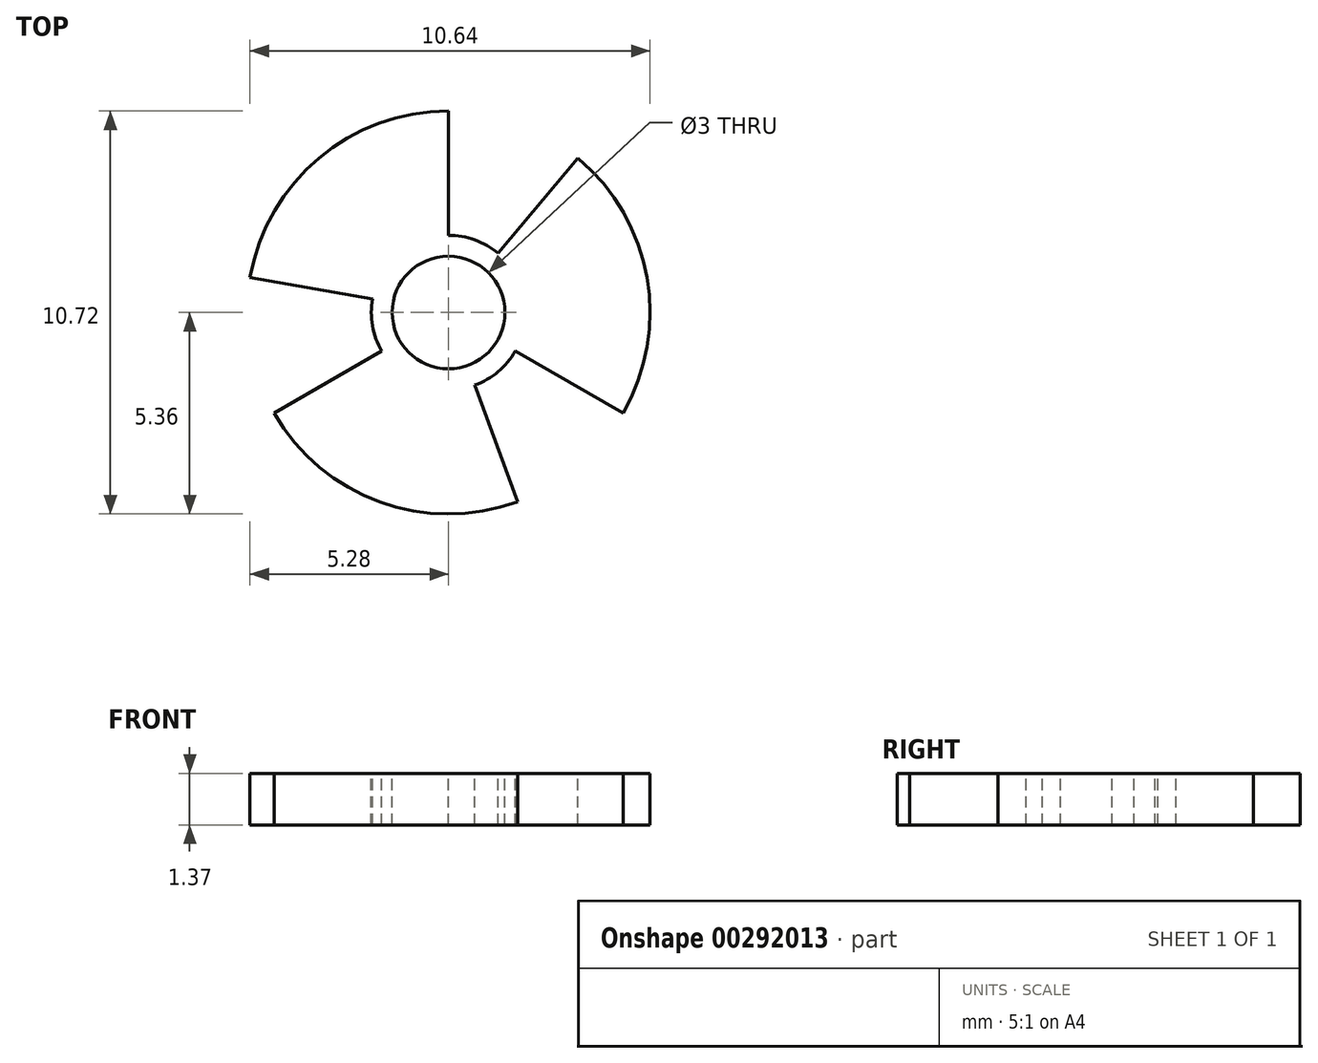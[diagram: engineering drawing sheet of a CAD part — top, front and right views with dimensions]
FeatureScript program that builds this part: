
annotation { "Feature Type Name" : "Feature", "Feature Type Description" : "" }
export const myFeature = defineFeature(function(context is Context, id is Id, definition is map)
    precondition{}
    {
        {
            var Q0;
            Q0=qCreatedBy(makeId("Top.planeOp"),FACE);
            var sketch = newSketch(context, id + "F0", { "sketchPlane" : qUnion([Q0])});
            skCircle(sketch, "E0", {"center": v(-28.46, 15.68) * mm, "radius": 28.38 * mm});
            skSolve(sketch);
        }
        {
            var Q0;
            Q0=makeQuery(id+"F0.imprint","IMPRINT",FACE,{"disambiguationData":[TD([[makeQuery(id+"F0.imprint","IMPRINT",EDGE,{"derivedFrom":sQuery(id+"F0.wireOp",EDGE,"E0")}),1.0]])]});
            var Q1;
            Q1=sQuery(id+"F0.wireOp",EDGE,"E0");
            extrude(context, id + "F1", {"entities" : qUnion([Q0]), "surfaceEntities" : qUnion([Q1]), "depth" : 8.64 * mm});
        }
        {
            var Q0;
            Q0=makeQuery(id+"F1.opExtrude","CAP_FACE",FACE,{"disambiguationData":[OSD([sQuery(id+"F0.wireOp",EDGE,"E0")])],"isStart":false});
            var sketch = newSketch(context, id + "F2", { "sketchPlane" : qUnion([Q0])});
            skCircle(sketch, "E1", {"center": v(-28.46, 15.68) * mm, "radius": 3.77 * mm});
            skSolve(sketch);
        }
        {
            var Q0;
            Q0=makeQuery(id+"F2.imprint","IMPRINT",FACE,{"disambiguationData":[TD([[makeQuery(id+"F2.imprint","IMPRINT",EDGE,{"derivedFrom":sQuery(id+"F2.wireOp",EDGE,"E1")}),1.0]])]});
            extrude(context, id + "F3", {"entities" : qUnion([Q0]), "operationType" : NewBodyOperationType.REMOVE, "oppositeDirection" : true, "depth" : 25.4 * mm});
        }
        {
            var Q0;
            Q0=makeQuery(id+"F1.opExtrude","SWEPT_BODY",BODY,{"disambiguationData":[OSD([sQuery(id+"F0.wireOp",EDGE,"E0")])]});
            deleteBodies(context, id + "F4", {"entities" : qUnion([Q0])});
        }
        {
            var Q0;
            Q0=qCreatedBy(makeId("Top.planeOp"),FACE);
            var sketch = newSketch(context, id + "F5", { "sketchPlane" : qUnion([Q0])});
            skCircle(sketch, "E2", {"center": v(0, 0) * mm, "radius": 5.36 * mm});
            skSolve(sketch);
        }
        {
            var Q0;
            Q0=makeQuery(id+"F5.imprint","IMPRINT",FACE,{"disambiguationData":[TD([[makeQuery(id+"F5.imprint","IMPRINT",EDGE,{"derivedFrom":sQuery(id+"F5.wireOp",EDGE,"E2")}),1.0]])]});
            extrude(context, id + "F6", {"entities" : qUnion([Q0]), "depth" : 1.37 * mm});
        }
        {
            var Q0;
            Q0=makeQuery(id+"F6.opExtrude","CAP_FACE",FACE,{"disambiguationData":[OSD([sQuery(id+"F5.wireOp",EDGE,"E2")])],"isStart":false});
            var sketch = newSketch(context, id + "F7", { "sketchPlane" : qUnion([Q0])});
            skCircle(sketch, "E3", {"center": v(0, 0) * mm, "radius": 1.5 * mm});
            skSolve(sketch);
        }
        {
            var Q0;
            Q0=makeQuery(id+"F7.imprint","IMPRINT",FACE,{"disambiguationData":[TD([[makeQuery(id+"F7.imprint","IMPRINT",EDGE,{"derivedFrom":sQuery(id+"F7.wireOp",EDGE,"E3")}),1.0]])]});
            extrude(context, id + "F8", {"entities" : qUnion([Q0]), "operationType" : NewBodyOperationType.REMOVE, "oppositeDirection" : true, "depth" : 25.4 * mm});
        }
        {
            var Q0;
            Q0=makeQuery(id+"F6.opExtrude","CAP_FACE",FACE,{"disambiguationData":[OSD([sQuery(id+"F5.wireOp",EDGE,"E2")])],"isStart":false});
            var sketch = newSketch(context, id + "F9", { "sketchPlane" : qUnion([Q0])});
            skCircle(sketch, "E4", {"center": v(0, 0) * mm, "radius": 2.05 * mm});
            skLineSegment(sketch, "E5", {"start": v(0, 2.05) * mm, "end": v(0, 5.36) * mm});
            skLineSegment(sketch, "E6.1.0", {"start": v(-1.32, 1.57) * mm, "end": v(-3.45, 4.1) * mm});
            skLineSegment(sketch, "E6.2.0", {"start": v(-2.02, 0.36) * mm, "end": v(-5.28, 0.93) * mm});
            skLineSegment(sketch, "E6.3.0", {"start": v(-1.78, -1.03) * mm, "end": v(-4.64, -2.68) * mm});
            skLineSegment(sketch, "E6.4.0", {"start": v(-0.7, -1.93) * mm, "end": v(-1.83, -5.04) * mm});
            skLineSegment(sketch, "E6.5.0", {"start": v(0.7, -1.93) * mm, "end": v(1.83, -5.04) * mm});
            skLineSegment(sketch, "E6.6.0", {"start": v(1.78, -1.03) * mm, "end": v(4.64, -2.68) * mm});
            skLineSegment(sketch, "E6.7.0", {"start": v(2.02, 0.36) * mm, "end": v(5.28, 0.93) * mm});
            skLineSegment(sketch, "E6.8.0", {"start": v(1.32, 1.57) * mm, "end": v(3.45, 4.1) * mm});
            skSolve(sketch);
        }
        {
            var Q0;
            {var subQ0=sQuery(id+"F9.wireOp",EDGE,"E6.5.0");Q0=makeQuery(id+"F9.imprint","IMPRINT",FACE,{"disambiguationData":[TD([[makeQuery(id+"F9.imprint","IMPRINT",EDGE,{"derivedFrom":subQ0}),1.0]])]});}
            var Q1;
            {var subQ0=sQuery(id+"F9.wireOp",EDGE,"E6.2.0");Q1=makeQuery(id+"F9.imprint","IMPRINT",FACE,{"disambiguationData":[TD([[makeQuery(id+"F9.imprint","IMPRINT",EDGE,{"derivedFrom":subQ0}),1.0]])]});}
            var Q2;
            {var subQ0=sQuery(id+"F9.wireOp",EDGE,"E5");Q2=makeQuery(id+"F9.imprint","IMPRINT",FACE,{"disambiguationData":[TD([[makeQuery(id+"F9.imprint","IMPRINT",EDGE,{"derivedFrom":subQ0}),-1.0]])]});}
            extrude(context, id + "F10", {"entities" : qUnion([Q0, Q1, Q2]), "operationType" : NewBodyOperationType.REMOVE, "oppositeDirection" : true, "depth" : 25.4 * mm});
        }
    });
